# Revit family: ITK_Кросс оптический_19-дюймовое крепление_2U
name_source: partatom
category: Обобщенные модели
units: mm (PartAtom-declared; Revit-internal decimal feet)

## family parameters
Всегда вертикально = Да
Может служить основой для арматурных стержней = Нет
На основе рабочей плоскости = Нет
Общий = Нет
При загрузке вырезать с полостями = Нет
Размер круглого соединителя = Использовать диаметр
Тип детали = Нормальный
Точка расчета площади = Нет

## types (1)
- FOBX48-2U-000
    ADSK_URL страницы изделия = https://www.itk-group.ru
    ADSK_Версия Revit = 2019
    ADSK_Версия семейства = 1.0
    ADSK_Группирование = I. ЩИТЫ И ПУЛЬТЫ
    ADSK_Единица измерения = шт
    ADSK_Завод-изготовитель = IEK
    ADSK_Код изделия = FOBX48-2U-000
    ADSK_Масса = 3
    ADSK_Материал наименование = Листовая сталь
    ADSK_Наименование = ITK 2U Оптический распределительный кросс до 48 портов (без планок, под 8п-6шт)
    IEK_URL = https://www.itk-group.ru
    IEK_Описание = Высокое качество материалов.
Увеличенный срок эксплуатации.
Надежная защита волокон от внешних механических воздействий и попадания внутрь посторонних предметов.
Соответствие международным стандартам и ГОСТ Р.
Удобство монтажа и эксплуатации.
    IEK_Цена за единицу = 2741.45
    KSI_CMa_Строительные материалы = 10.03.02.06
    KSI_CPr_Строительные изделия = 26.30.40.61.1.04.09-1081 26.30.40.61.1.04.09-1082 26.30.40.61.1.04.09-1083
    URL = https://www.iek.ru
    Изготовитель = ITK
    Тип монтажа = 19-дюймовое крепление
